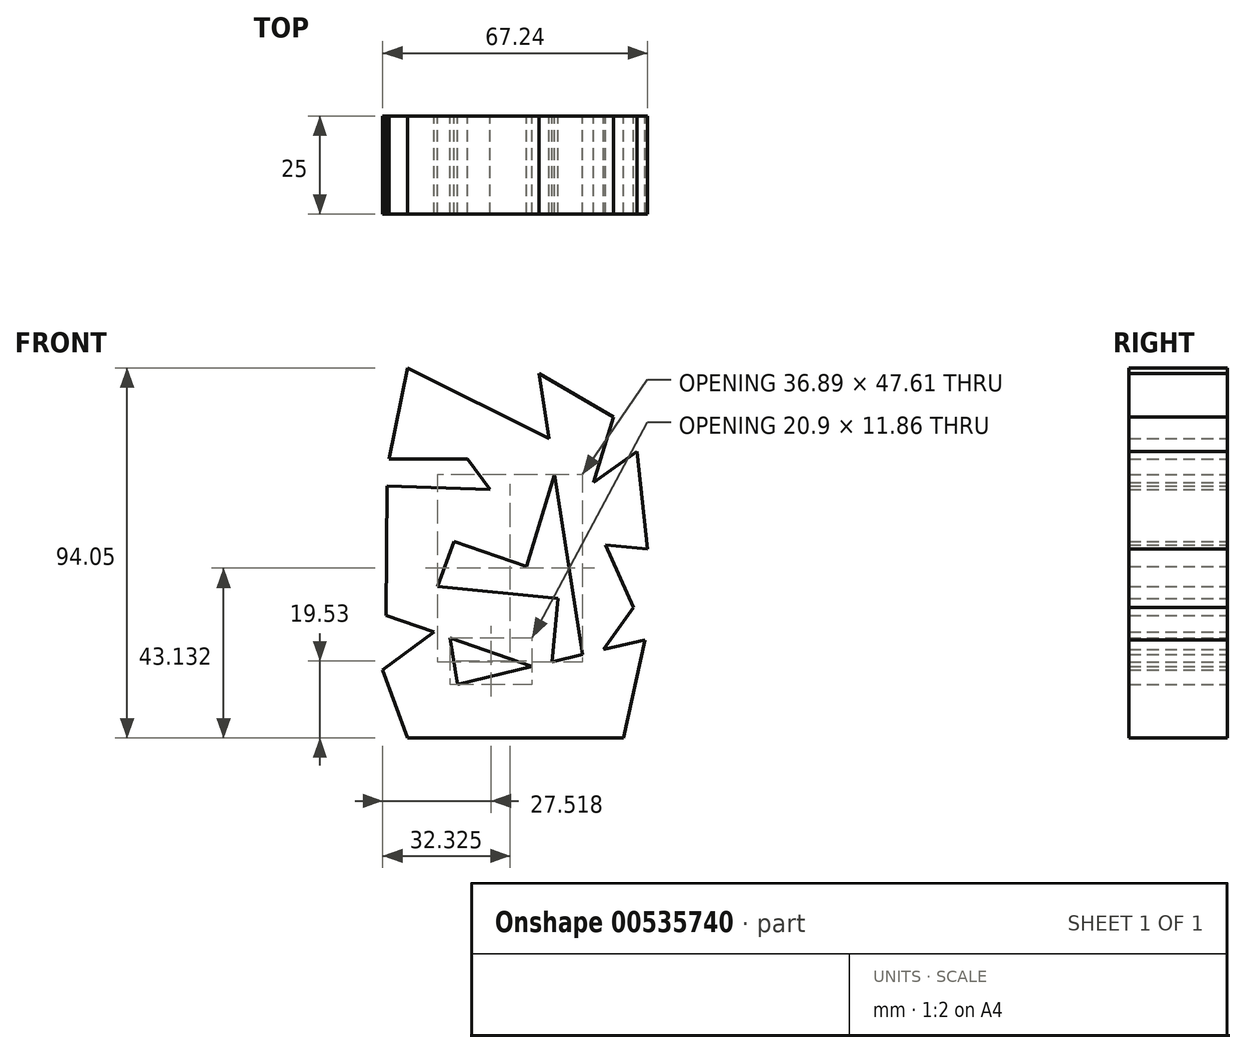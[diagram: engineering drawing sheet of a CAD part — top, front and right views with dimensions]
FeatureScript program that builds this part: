
annotation { "Feature Type Name" : "Feature", "Feature Type Description" : "" }
export const myFeature = defineFeature(function(context is Context, id is Id, definition is map)
    precondition{}
    {
        {
            var Q0;
            Q0=qCreatedBy(makeId("Front.planeOp"),FACE);
            var sketch = newSketch(context, id + "F0", { "sketchPlane" : qUnion([Q0])});
            skLineSegment(sketch, "E0", {"start": v(-30.31, 41.36) * mm, "end": v(9.34, 21.54) * mm});
            skLineSegment(sketch, "E1", {"start": v(9.34, 21.54) * mm, "end": v(0, -9.06) * mm});
            skLineSegment(sketch, "E2", {"start": v(0, -9.06) * mm, "end": v(-18.41, -2.83) * mm});
            skLineSegment(sketch, "E3", {"start": v(-18.41, -2.83) * mm, "end": v(-22.66, -14.16) * mm});
            skLineSegment(sketch, "E4", {"start": v(-22.66, -14.16) * mm, "end": v(7.93, -17.28) * mm});
            skLineSegment(sketch, "E5", {"start": v(7.93, -17.28) * mm, "end": v(6.23, -36.26) * mm});
            skLineSegment(sketch, "E6", {"start": v(6.23, -36.26) * mm, "end": v(-35.7, -21.53) * mm});
            skLineSegment(sketch, "E7", {"start": v(-35.7, -21.53) * mm, "end": v(-35.4, 11.33) * mm});
            skLineSegment(sketch, "E8", {"start": v(-35.4, 11.33) * mm, "end": v(-9.35, 10.48) * mm});
            skLineSegment(sketch, "E9", {"start": v(-9.35, 10.48) * mm, "end": v(-15.01, 18.13) * mm});
            skLineSegment(sketch, "E10", {"start": v(-15.01, 18.13) * mm, "end": v(-34.9, 18.13) * mm});
            skLineSegment(sketch, "E11", {"start": v(-34.9, 18.13) * mm, "end": v(-30.31, 41.36) * mm});
            skLineSegment(sketch, "E12", {"start": v(3.12, 39.94) * mm, "end": v(15.01, -36.54) * mm});
            skLineSegment(sketch, "E13", {"start": v(15.01, -36.54) * mm, "end": v(27.2, -19.55) * mm});
            skLineSegment(sketch, "E14", {"start": v(27.2, -19.55) * mm, "end": v(20.1, -3.72) * mm});
            skLineSegment(sketch, "E15", {"start": v(20.1, -3.72) * mm, "end": v(30.7, -4.67) * mm});
            skLineSegment(sketch, "E16", {"start": v(30.7, -4.67) * mm, "end": v(28.04, 20.11) * mm});
            skLineSegment(sketch, "E17", {"start": v(28.04, 20.11) * mm, "end": v(17, 12.18) * mm});
            skLineSegment(sketch, "E18", {"start": v(17, 12.18) * mm, "end": v(22.1, 28.9) * mm});
            skLineSegment(sketch, "E19", {"start": v(22.1, 28.9) * mm, "end": v(3.12, 39.94) * mm});
            skLineSegment(sketch, "E20", {"start": v(-36.54, -35.4) * mm, "end": v(-20.11, -23.23) * mm});
            skLineSegment(sketch, "E21", {"start": v(-20.11, -23.23) * mm, "end": v(-17.56, -39.1) * mm});
            skLineSegment(sketch, "E22", {"start": v(-17.56, -39.1) * mm, "end": v(30.03, -27.76) * mm});
            skLineSegment(sketch, "E23", {"start": v(30.03, -27.76) * mm, "end": v(24.64, -52.69) * mm});
            skLineSegment(sketch, "E24", {"start": v(24.64, -52.69) * mm, "end": v(-30.31, -52.69) * mm});
            skLineSegment(sketch, "E25", {"start": v(-30.31, -52.69) * mm, "end": v(-36.54, -35.4) * mm});
            skPoint(sketch, "E26", {"position": v(6.23, -33.43) * mm});
            skSolve(sketch);
        }
        {
            var Q0;
            {var subQ0=sQuery(id+"F0.wireOp",EDGE,"E1");var subQ1=sQuery(id+"F0.wireOp",EDGE,"E0");var subQ2=makeQuery(id+"F0.imprint","INTERSECT",VERTEX,{"derivedFrom":[subQ1,subQ0]});Q0=makeQuery(id+"F0.imprint","IMPRINT",FACE,{"disambiguationData":[TD([[makeQuery(id+"F0.imprint","IMPRINT",EDGE,{"disambiguationData":[TD([[subQ2,1.0]])],"derivedFrom":subQ1}),-1.0]])]});}
            var Q1;
            {var subQ0=sQuery(id+"F0.wireOp",EDGE,"E14");Q1=makeQuery(id+"F0.imprint","IMPRINT",FACE,{"disambiguationData":[TD([[makeQuery(id+"F0.imprint","IMPRINT",EDGE,{"derivedFrom":subQ0}),1.0]])]});}
            var Q2;
            {var subQ0=sQuery(id+"F0.wireOp",EDGE,"E5");var subQ1=sQuery(id+"F0.wireOp",EDGE,"E4");var subQ2=makeQuery(id+"F0.imprint","INTERSECT",VERTEX,{"derivedFrom":[subQ1,subQ0]});Q2=makeQuery(id+"F0.imprint","IMPRINT",FACE,{"disambiguationData":[TD([[makeQuery(id+"F0.imprint","IMPRINT",EDGE,{"disambiguationData":[TD([[subQ2,1.0]])],"derivedFrom":subQ1}),-1.0]])]});}
            var Q3;
            {var subQ19=sQuery(id+"F0.wireOp",EDGE,"E2");Q3=makeQuery(id+"F0.imprint","IMPRINT",FACE,{"disambiguationData":[TD([[makeQuery(id+"F0.imprint","IMPRINT",EDGE,{"derivedFrom":subQ19}),-1.0]])]});}
            var Q4;
            {var subQ0=sQuery(id+"F0.wireOp",EDGE,"E20");var subQ1=sQuery(id+"F0.wireOp",EDGE,"E6");var subQ2=makeQuery(id+"F0.imprint","INTERSECT",VERTEX,{"derivedFrom":[subQ1,subQ0]});Q4=makeQuery(id+"F0.imprint","IMPRINT",FACE,{"disambiguationData":[TD([[makeQuery(id+"F0.imprint","IMPRINT",EDGE,{"disambiguationData":[TD([[subQ2,1.0]])],"derivedFrom":subQ1}),-1.0]])]});}
            var Q5;
            {var subQ0=sQuery(id+"F0.wireOp",EDGE,"E13");var subQ1=sQuery(id+"F0.wireOp",EDGE,"E12");var subQ2=makeQuery(id+"F0.imprint","INTERSECT",VERTEX,{"derivedFrom":[subQ1,subQ0]});Q5=makeQuery(id+"F0.imprint","IMPRINT",FACE,{"disambiguationData":[TD([[makeQuery(id+"F0.imprint","IMPRINT",EDGE,{"disambiguationData":[TD([[subQ2,1.0]])],"derivedFrom":subQ1}),1.0]])]});}
            var Q6;
            {var subQ0=sQuery(id+"F0.wireOp",EDGE,"E6");var subQ1=sQuery(id+"F0.wireOp",EDGE,"E5");var subQ2=makeQuery(id+"F0.imprint","INTERSECT",VERTEX,{"derivedFrom":[subQ1,subQ0]});Q6=makeQuery(id+"F0.imprint","IMPRINT",FACE,{"disambiguationData":[TD([[makeQuery(id+"F0.imprint","IMPRINT",EDGE,{"disambiguationData":[TD([[subQ2,1.0]])],"derivedFrom":subQ1}),-1.0]])]});}
            var Q7;
            {var subQ0=sQuery(id+"F0.wireOp",EDGE,"E23");Q7=makeQuery(id+"F0.imprint","IMPRINT",FACE,{"disambiguationData":[TD([[makeQuery(id+"F0.imprint","IMPRINT",EDGE,{"derivedFrom":subQ0}),-1.0]])]});}
            extrude(context, id + "F1", {"entities" : qUnion([Q0, Q1, Q2, Q3, Q4, Q5, Q6, Q7]), "depth" : 25 * mm, "offsetDistance" : 25 * mm});
        }
    });
